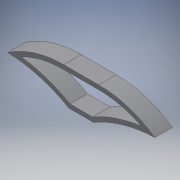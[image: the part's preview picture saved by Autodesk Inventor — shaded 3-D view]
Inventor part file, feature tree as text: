
AUTODESK INVENTOR PART (.ipt)
format: ipt  version: 2016 SP2 (Build 200236200, 236)  size: 112,640 bytes
history: native  units: mm
features: extrude x1, sketch x1
ambient origin geometry x8: Origin, YZ Plane, XZ Plane, XY Plane, X Axis, Y Axis, Z Axis, Center Point
bodies: Volumenkörper1 (feature_tree)
feature tree (2):
  extrude  "Extrusion1"  Depth=5.0mm
  sketch  "Skizze1"  dims[d0=5.0mm d1=21.0mm d2=5.0mm d3=5.0mm d4=5.0mm d6=1.2mm d7=10.0mm d8=5.0mm d9=0.0mm]
